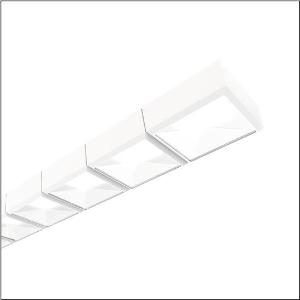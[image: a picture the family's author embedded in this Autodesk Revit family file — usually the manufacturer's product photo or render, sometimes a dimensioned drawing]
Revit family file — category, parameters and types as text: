
# Revit family: scriptus_r__11_5mz314d04wa_e059
name_source: partatom
category: Lighting Fixtures
units: mm (PartAtom-declared; Revit-internal decimal feet)

## family parameters
Cut with Voids When Loaded = No
Host = Face
Light Source = No
Part Type = Normal
Room Calculation Point = No
Round Connector Dimension = Use Diameter
Shared = No

## types (1)
- Scriptus® 11 (1 x LED 4000K / CRI = 80 (unbekannt), 3220 lm / 4820 lm, 4000K)
    Apparent Load = 120 VA
    CIE Flux Codes = - - - 0 100 / 82 95 99 100 100
    Color Rendering = 80
    Color Temperature = 4000K
    Default Elevation = 1800 mm
    Description = Scriptus® 11, office luminaire, primary optical cover: lenses, CAT 2 (L<= 3000cd/m²), light emission: direct/indirect distribution, primary light characteristic: symmetric, installation type: suspended mounting, LED, rated luminous flux: 16.060lm, luminous efficacy: 133lm/W, light colour: 840, colour temperature: 4000K, control gear: ECG DALI, with terminal, 5-pole, mains connection: 230V, AC, 50Hz, rated input power: 120W, LED, control gear: ECG DALI, housing, luminaire housing, of aluminium, traffic white (RAL 9016), length: 3.088mm, width: 114mm, height: 57mm, protection rating (complete): IP20, insulation class (complete): insulation class I (protective earthing), certification: CE, ENEC, VDE, protection symbol: F, permissible operating ambient temperature: 0..+35°C, standard: EN 50419, packaging unit: 1 piece
    Height = 57 mm
    Lamp = 1 x LED 4000K / CRI >= 80 (unbekannt)
    Lamp Light Flux = 3220 lm / 4820 lm
    Lamp count = 1
    Length = 3088 mm
    Luminous efficacy = 134 lm/W
    Manufacturer = Siteco
    ModVariant = No
    Model = 5MZ314D04WA
    Mounting Place = Ceiling
    Mounting Type = Pendant
    Number of Poles = 1
    OnlyDefault = Yes
    Power Factor = 1
    Product Name = Scriptus® 11
    Product group = office luminaire | ceiling pendant
    ProductGroupID = 902
    Protection Class = Protection class I
    Protection Degree = IP 20
    RLX_Detail_Level = 1
    RLX_Emergency_Light_Flux = 0 lm
    RLX_Emergency_Type = 0
    RLX_Emergency_Type_DB = No
    RlxData = <blob elided: 31925 chars, md5=c801790a>
    Socket = socket
    Standby Power = 0 W
    System Light Flux = 16080 lm
    System Power = 120 W
    Type Comments = Product without accessories
    Type Image = l_1004839.jpg
    URL = http://relux.com
    VarID = ---
    Voltage = 0 V
    Weight = 0.00 kg
    Width = 114 mm

## geometry (parser evidence)
native form markers: Blend x4, Sweep x19
no freeform markers — native parametric forms only
